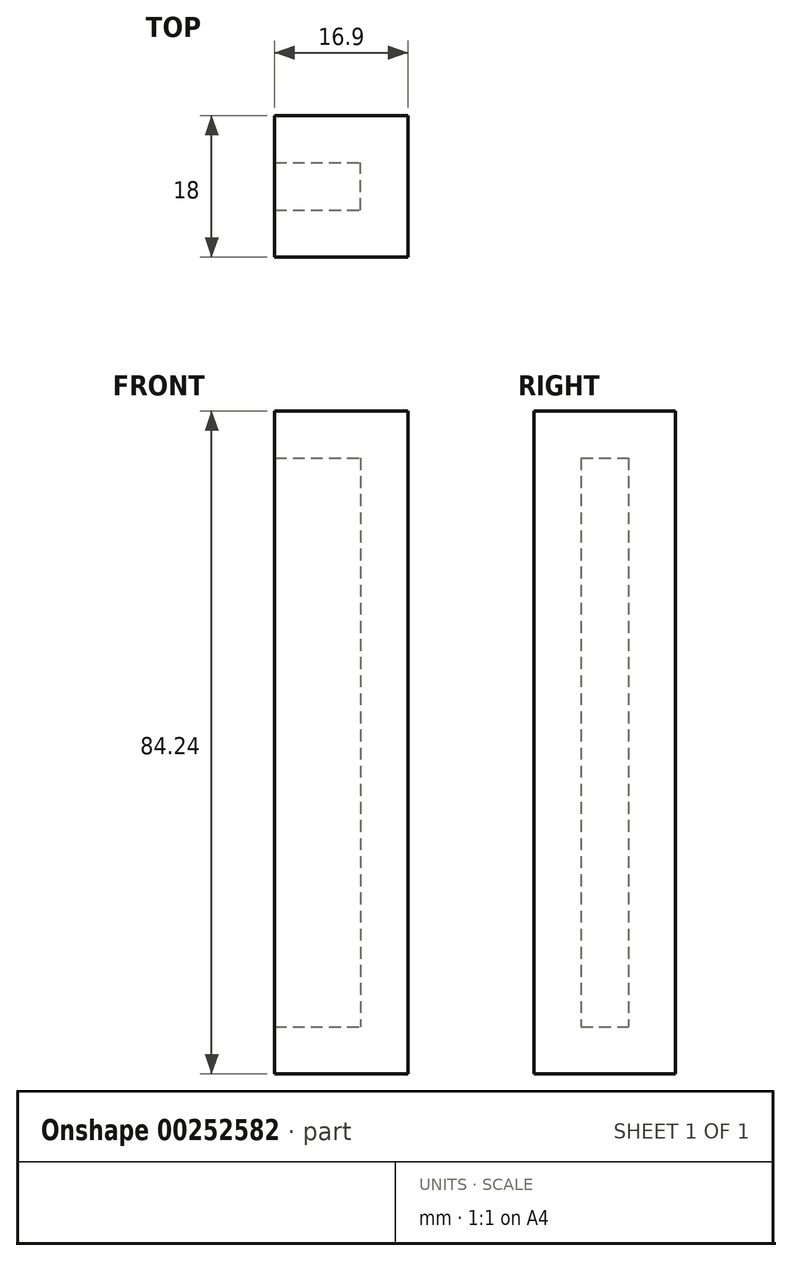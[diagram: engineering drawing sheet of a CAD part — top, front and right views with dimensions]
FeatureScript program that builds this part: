
annotation { "Feature Type Name" : "Feature", "Feature Type Description" : "" }
export const myFeature = defineFeature(function(context is Context, id is Id, definition is map)
    precondition{}
    {
        {
            var Q0;
            Q0=qCreatedBy(makeId("Front.planeOp"),FACE);
            var sketch = newSketch(context, id + "F0", { "sketchPlane" : qUnion([Q0])});
            skLineSegment(sketch, "E0.bottom", {"start": v(-8.45, 42.12) * mm, "end": v(8.45, 42.12) * mm});
            skLineSegment(sketch, "E0.top", {"start": v(-8.45, -42.12) * mm, "end": v(8.45, -42.12) * mm});
            skLineSegment(sketch, "E0.left", {"start": v(-8.45, 42.12) * mm, "end": v(-8.45, -42.12) * mm});
            skLineSegment(sketch, "E0.right", {"start": v(8.45, 42.12) * mm, "end": v(8.45, -42.12) * mm});
            skPoint(sketch, "E0.middle", {"position": v(0, 0) * mm});
            skSolve(sketch);
        }
        {
            var Q0;
            Q0=makeQuery(id+"F0.imprint","IMPRINT",FACE,{"disambiguationData":[TD([[makeQuery(id+"F0.imprint","IMPRINT",EDGE,{"derivedFrom":sQuery(id+"F0.wireOp",EDGE,"E0.bottom")}),-1.0]])]});
            extrude(context, id + "F1", {"entities" : qUnion([Q0]), "depth" : 18 * mm});
        }
        {
            var Q0;
            Q0=makeQuery(id+"F1.opExtrude","SWEPT_FACE",FACE,{"disambiguationData":[OSD([sQuery(id+"F0.wireOp",EDGE,"E0.left")])]});
            shell(context, id + "F2", {"entities" : qUnion([Q0]), "thickness" : 6 * mm});
        }
    });
